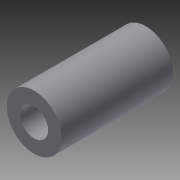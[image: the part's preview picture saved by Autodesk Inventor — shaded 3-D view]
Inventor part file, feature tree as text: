
AUTODESK INVENTOR PART (.ipt)
format: ipt  version: 2015 SP1 (Build 190203100, 203)  size: 82,944 bytes
history: native  units: in
note: dims shown in document units (in); Inventor stores cm internally (conversion verified against a paired STEP export)
features: extrude x1, other x1
ambient origin geometry x8: Origin, YZ Plane, XZ Plane, XY Plane, X Axis, Y Axis, Z Axis, Center Point
bodies: Solid1 (feature_tree)
feature tree (2):
  extrude  "profile_extrusion"  Depth=0.25in
  other  "profile_sketch"
